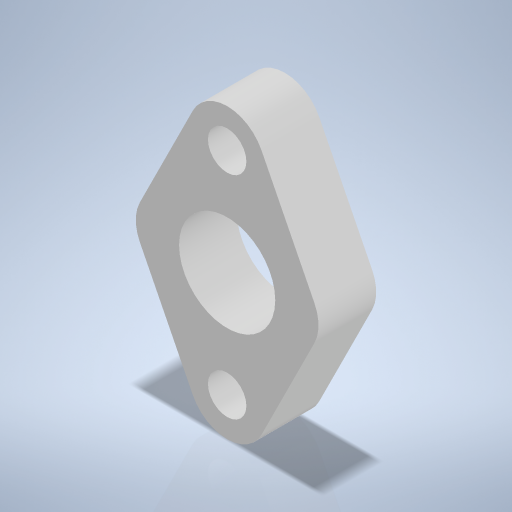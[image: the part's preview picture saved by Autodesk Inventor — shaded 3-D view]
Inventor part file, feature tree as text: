
AUTODESK INVENTOR PART (.ipt)
format: ipt  version: 2024 (Build 280153000, 153)  size: 269,312 bytes
history: native  units: mm
features: sketch x3, hole x2, extrude x1
ambient origin geometry x8: Origin, YZ Plane, XZ Plane, XY Plane, X Axis, Y Axis, Z Axis, Center Point
bodies: Volumenkörper1 (feature_tree)
feature tree (6):
  extrude  "Extrusion1"  Depth=22.0mm
  hole  "Bohrung1"  [1 undecoded]
  hole  "Bohrung2"  [1 undecoded]
  sketch  "Skizze1"  dims[d4=19.0mm d5=22.0mm]
  sketch  "Skizze2"  dims[d6=4.0mm d7=4.0mm]
  sketch  "Skizze3"  dims[d8=4.0mm d9=4.0mm d10=30.0mm d11=6.0mm d12=0.0mm d13=4.0mm d14=6.0mm d15=4.0mm d16=2.0mm d17=90.0deg d18=8.0mm d19=20.594885mm d20=10.0mm d21=6.0mm d22=4.0mm d23=2.0mm d24=90.0deg d25=8.0mm d26=20.594885mm]
note: 2 required parameter values undecoded (feature->parameter linkage not recoverable at this tier; creation-order binding heuristic only, values carry confidence <= 0.55)
